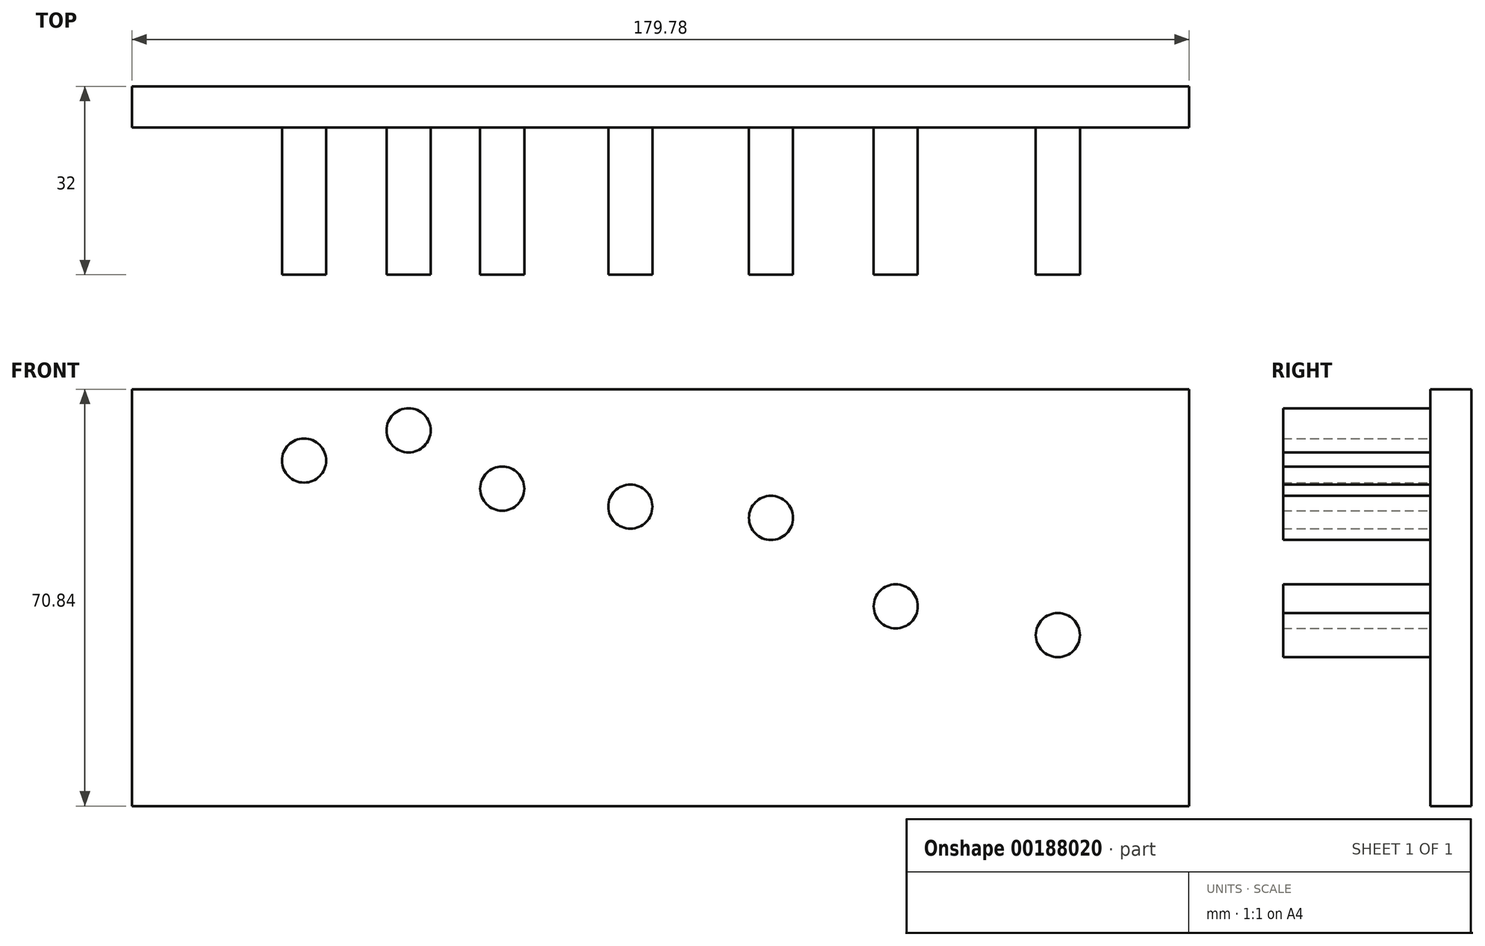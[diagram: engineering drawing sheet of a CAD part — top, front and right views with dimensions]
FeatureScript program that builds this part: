
annotation { "Feature Type Name" : "Feature", "Feature Type Description" : "" }
export const myFeature = defineFeature(function(context is Context, id is Id, definition is map)
    precondition{}
    {
        {
            var Q0;
            Q0=qCreatedBy(makeId("Front.planeOp"),FACE);
            var sketch = newSketch(context, id + "F0", { "sketchPlane" : qUnion([Q0])});
            skLineSegment(sketch, "E0.bottom", {"start": v(-90.98, 58.39) * mm, "end": v(88.8, 58.39) * mm});
            skLineSegment(sketch, "E0.top", {"start": v(-90.98, -12.45) * mm, "end": v(88.8, -12.45) * mm});
            skLineSegment(sketch, "E0.left", {"start": v(-90.98, 58.39) * mm, "end": v(-90.98, -12.45) * mm});
            skLineSegment(sketch, "E0.right", {"start": v(88.8, 58.39) * mm, "end": v(88.8, -12.45) * mm});
            skSolve(sketch);
        }
        {
            var Q0;
            Q0=qSketchRegion(id+"F0",true);
            extrude(context, id + "F1", {"entities" : qUnion([Q0]), "depth" : 7 * mm});
        }
        {
            var Q0;
            Q0=makeQuery(id+"F1.opExtrude","CAP_FACE",FACE,{"disambiguationData":[OSD([sQuery(id+"F0.wireOp",EDGE,"E0.bottom"),sQuery(id+"F0.wireOp",EDGE,"E0.top"),sQuery(id+"F0.wireOp",EDGE,"E0.left"),sQuery(id+"F0.wireOp",EDGE,"E0.right")])],"isStart":false});
            var sketch = newSketch(context, id + "F2", { "sketchPlane" : qUnion([Q0])});
            skCircle(sketch, "E1", {"center": v(-61.7, 46.28) * mm, "radius": 3.75 * mm});
            skSolve(sketch);
        }
        {
            var Q0;
            Q0=qSketchRegion(id+"F2",true);
            extrude(context, id + "F3", {"entities" : qUnion([Q0]), "operationType" : NewBodyOperationType.ADD, "depth" : 25 * mm});
        }
        {
            var Q0;
            Q0=makeQuery(id+"F1.opExtrude","CAP_FACE",FACE,{"disambiguationData":[OSD([sQuery(id+"F0.wireOp",EDGE,"E0.bottom"),sQuery(id+"F0.wireOp",EDGE,"E0.top"),sQuery(id+"F0.wireOp",EDGE,"E0.left"),sQuery(id+"F0.wireOp",EDGE,"E0.right")])],"isStart":false});
            var sketch = newSketch(context, id + "F4", { "sketchPlane" : qUnion([Q0])});
            skCircle(sketch, "E2", {"center": v(-43.92, 51.41) * mm, "radius": 3.75 * mm});
            skSolve(sketch);
        }
        {
            var Q0;
            Q0=qSketchRegion(id+"F4",true);
            extrude(context, id + "F5", {"entities" : qUnion([Q0]), "operationType" : NewBodyOperationType.ADD, "depth" : 25 * mm});
        }
        {
            var Q0;
            Q0=makeQuery(id+"F1.opExtrude","CAP_FACE",FACE,{"disambiguationData":[OSD([sQuery(id+"F0.wireOp",EDGE,"E0.bottom"),sQuery(id+"F0.wireOp",EDGE,"E0.top"),sQuery(id+"F0.wireOp",EDGE,"E0.left"),sQuery(id+"F0.wireOp",EDGE,"E0.right")])],"isStart":false});
            var sketch = newSketch(context, id + "F6", { "sketchPlane" : qUnion([Q0])});
            skCircle(sketch, "E3", {"center": v(-28, 41.5) * mm, "radius": 3.75 * mm});
            skSolve(sketch);
        }
        {
            var Q0;
            Q0=qSketchRegion(id+"F6",true);
            extrude(context, id + "F7", {"entities" : qUnion([Q0]), "operationType" : NewBodyOperationType.ADD, "depth" : 25 * mm});
        }
        {
            var Q0;
            Q0=makeQuery(id+"F1.opExtrude","CAP_FACE",FACE,{"disambiguationData":[OSD([sQuery(id+"F0.wireOp",EDGE,"E0.bottom"),sQuery(id+"F0.wireOp",EDGE,"E0.top"),sQuery(id+"F0.wireOp",EDGE,"E0.left"),sQuery(id+"F0.wireOp",EDGE,"E0.right")])],"isStart":false});
            var sketch = newSketch(context, id + "F8", { "sketchPlane" : qUnion([Q0])});
            skCircle(sketch, "E4", {"center": v(-6.21, 38.45) * mm, "radius": 3.75 * mm});
            skSolve(sketch);
        }
        {
            var Q0;
            Q0=qSketchRegion(id+"F8",true);
            extrude(context, id + "F9", {"entities" : qUnion([Q0]), "operationType" : NewBodyOperationType.ADD, "depth" : 25 * mm});
        }
        {
            var Q0;
            Q0=makeQuery(id+"F1.opExtrude","CAP_FACE",FACE,{"disambiguationData":[OSD([sQuery(id+"F0.wireOp",EDGE,"E0.bottom"),sQuery(id+"F0.wireOp",EDGE,"E0.top"),sQuery(id+"F0.wireOp",EDGE,"E0.left"),sQuery(id+"F0.wireOp",EDGE,"E0.right")])],"isStart":false});
            var sketch = newSketch(context, id + "F10", { "sketchPlane" : qUnion([Q0])});
            skCircle(sketch, "E5", {"center": v(17.71, 36.53) * mm, "radius": 3.75 * mm});
            skSolve(sketch);
        }
        {
            var Q0;
            Q0=qSketchRegion(id+"F10",true);
            extrude(context, id + "F11", {"entities" : qUnion([Q0]), "operationType" : NewBodyOperationType.ADD, "depth" : 25 * mm});
        }
        {
            var Q0;
            Q0=makeQuery(id+"F1.opExtrude","CAP_FACE",FACE,{"disambiguationData":[OSD([sQuery(id+"F0.wireOp",EDGE,"E0.bottom"),sQuery(id+"F0.wireOp",EDGE,"E0.top"),sQuery(id+"F0.wireOp",EDGE,"E0.left"),sQuery(id+"F0.wireOp",EDGE,"E0.right")])],"isStart":false});
            var sketch = newSketch(context, id + "F12", { "sketchPlane" : qUnion([Q0])});
            skCircle(sketch, "E6", {"center": v(38.92, 21.5) * mm, "radius": 3.75 * mm});
            skSolve(sketch);
        }
        {
            var Q0;
            Q0=qSketchRegion(id+"F12",true);
            extrude(context, id + "F13", {"entities" : qUnion([Q0]), "operationType" : NewBodyOperationType.ADD, "depth" : 25 * mm});
        }
        {
            var Q0;
            Q0=makeQuery(id+"F1.opExtrude","CAP_FACE",FACE,{"disambiguationData":[OSD([sQuery(id+"F0.wireOp",EDGE,"E0.bottom"),sQuery(id+"F0.wireOp",EDGE,"E0.top"),sQuery(id+"F0.wireOp",EDGE,"E0.left"),sQuery(id+"F0.wireOp",EDGE,"E0.right")])],"isStart":false});
            var sketch = newSketch(context, id + "F14", { "sketchPlane" : qUnion([Q0])});
            skCircle(sketch, "E7", {"center": v(66.5, 16.6) * mm, "radius": 3.75 * mm});
            skSolve(sketch);
        }
        {
            var Q0;
            Q0=qSketchRegion(id+"F14",true);
            extrude(context, id + "F15", {"entities" : qUnion([Q0]), "operationType" : NewBodyOperationType.ADD, "depth" : 25 * mm});
        }
    });
